# Revit family: LED OLIVE 02_LZE11WW
name_source: partatom
category: Luminarias
units: mm (PartAtom-declared; Revit-internal decimal feet)

## family parameters
Compartido = No
Corte con vacíos al cargar = No
Cota de conector redondo = Diámetro de uso
Origen de luz = Sí
Punto de cálculo de habitación = No
Se basa en plano de trabajo = Sí
Siempre vertical = No
Tipo de pieza = Normal

## types (1)
- LED OLIVE 02_LZE11WW
    Cambio de temperatura de color de luz atenuada = <Ninguno>
    Comentarios de vataje = 90-240V
    Descripción = LUMINARIA TIPO CORTESIA TIPO CIRCULAR PARA EMPOTRAR EN MURO CON CUERPO DE ALUMINIO, IP 20 USO PARA INTERIORES, CUENTA CON 1 LED TIPO CREE CON UNA POTENCIA TOTAL DE 4W, A UNA TEMPERATURA EN BLANCO CALIDO 3000K CON 144 LUMENES, EFICIENCIA DE 36LM/W, IRC 80, APERTURA A 45 GRADOS EN STOCK, CABLE 0.5M CON FUENTE EXTERNA REMOTA (INCLUIDA) ALIMENTADA A 90-240V.
    Elevación por defecto = 0 mm  [stored 0 ft]
    Fabricante = BRILLANT
    Filtro de color = 16777215
    Lámpara = Cree
    Modelo = LZE11WW
    Tamaño de símbolo de origen de luz = 100 mm  [stored 0.328084 ft]
    Watt per fixture = 4

note: [stored X ft] marks values corroborated as IEEE doubles in the binary element streams (Revit-internal decimal feet)

## geometry (parser evidence)
native form markers: Blend x2
no freeform markers — native parametric forms only
